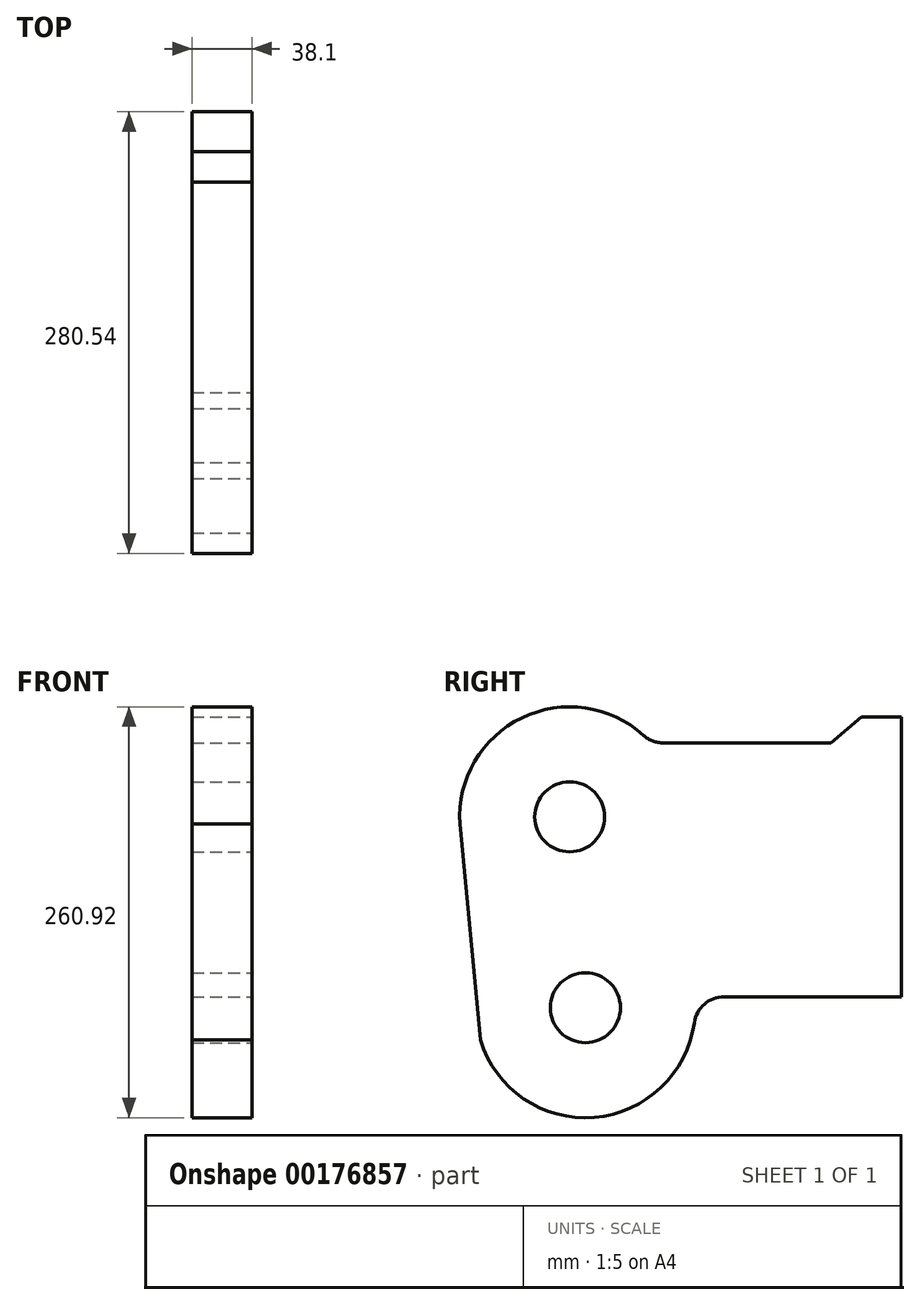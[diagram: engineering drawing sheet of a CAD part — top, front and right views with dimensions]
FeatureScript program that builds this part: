
annotation { "Feature Type Name" : "Feature", "Feature Type Description" : "" }
export const myFeature = defineFeature(function(context is Context, id is Id, definition is map)
    precondition{}
    {
        {
            var Q0;
            Q0=qCreatedBy(makeId("Top.planeOp"),FACE);
            var sketch = newSketch(context, id + "F0", { "sketchPlane" : qUnion([Q0])});
            skLineSegment(sketch, "E0.bottom", {"start": v(-19.05, 0) * mm, "end": v(19.05, 0) * mm});
            skLineSegment(sketch, "E0.top", {"start": v(-19.05, -355.6) * mm, "end": v(19.05, -355.6) * mm});
            skLineSegment(sketch, "E0.left", {"start": v(-19.05, 0) * mm, "end": v(-19.05, -355.6) * mm});
            skLineSegment(sketch, "E0.right", {"start": v(19.05, 0) * mm, "end": v(19.05, -355.6) * mm});
            skSolve(sketch);
        }
        {
            var Q0;
            Q0 = qSketchRegion(id + "F0", true);
            extrude(context, id + "F1", {"entities" : qUnion([Q0]), "depth" : 101.6 * mm, "hasSecondDirection" : true, "secondDirectionOppositeDirection" : true, "secondDirectionDepth" : 190.5 * mm});
        }
        {
            var Q0;
            Q0=makeQuery(id+"F1.opExtrude","SWEPT_FACE",FACE,{"disambiguationData":[OSD([sQuery(id+"F0.wireOp",EDGE,"E0.right")])]});
            var sketch = newSketch(context, id + "F2", { "sketchPlane" : qUnion([Q0])});
            skCircle(sketch, "E1", {"center": v(-210.69, 25.4) * mm, "radius": 22.23 * mm});
            skArc(sketch, "E2", {"start": v(-163.87, 77.23) * mm, "mid": v(-241.06, 88.3) * mm, "end": v(-280.4, 20.96) * mm});
            skLineSegment(sketch, "E3", {"start": v(-151.1, 72.32) * mm, "end": v(-44.64, 72.32) * mm});
            skPoint(sketch, "E4.visualSharp", {"position": v(-158.94, 72.32) * mm});
            skArc(sketch, "E4.filletArc", {"start": v(-163.87, 77.23) * mm, "mid": v(-157.94, 73.6) * mm, "end": v(-151.1, 72.32) * mm});
            skCircle(sketch, "E5", {"center": v(-200.7, -95.82) * mm, "radius": 22.23 * mm});
            skArc(sketch, "E6", {"start": v(-267.46, -116.33) * mm, "mid": v(-195.07, -165.45) * mm, "end": v(-131.5, -105.35) * mm});
            skLineSegment(sketch, "E7", {"start": v(-280.4, 20.96) * mm, "end": v(-267.46, -116.33) * mm});
            skLineSegment(sketch, "E8", {"start": v(0, -88.9) * mm, "end": v(-112.62, -88.9) * mm});
            skPoint(sketch, "E9.visualSharp", {"position": v(-131.19, -88.9) * mm});
            skArc(sketch, "E9.filletArc", {"start": v(-112.62, -88.9) * mm, "mid": v(-125.14, -93.6) * mm, "end": v(-131.5, -105.35) * mm});
            skLineSegment(sketch, "E10", {"start": v(0, 0) * mm, "end": v(0, -88.9) * mm});
            skLineSegment(sketch, "E11", {"start": v(0, 0) * mm, "end": v(0, 88.9) * mm});
            skLineSegment(sketch, "E12", {"start": v(0, 88.9) * mm, "end": v(-25.4, 88.9) * mm});
            skLineSegment(sketch, "E13", {"start": v(-25.4, 88.9) * mm, "end": v(-44.64, 72.32) * mm});
            skSolve(sketch);
        }
        {
            var Q0;
            Q0=makeQuery(id+"F2.imprint","IMPRINT",FACE,{"disambiguationData":[TD([[makeQuery(id+"F2.imprint","IMPRINT",EDGE,{"derivedFrom":sQuery(id+"F2.wireOp",EDGE,"E1")}),1.0]])]});
            var Q1;
            Q1=makeQuery(id+"F2.imprint","IMPRINT",FACE,{"disambiguationData":[TD([[makeQuery(id+"F2.imprint","IMPRINT",EDGE,{"derivedFrom":sQuery(id+"F2.wireOp",EDGE,"E5")}),1.0]])]});
            var Q2;
            Q2=makeQuery(id+"F2.imprint","IMPRINT",FACE,{"disambiguationData":[TD([[makeQuery(id+"F2.imprint","IMPRINT",EDGE,{"derivedFrom":sQuery(id+"F2.wireOp",EDGE,"E2")}),-1.0]])]});
            extrude(context, id + "F3", {"entities" : qUnion([Q0, Q1, Q2]), "operationType" : NewBodyOperationType.REMOVE, "endBound" : BoundingType.SYMMETRIC, "oppositeDirection" : true, "depth" : 76.2 * mm});
        }
    });
